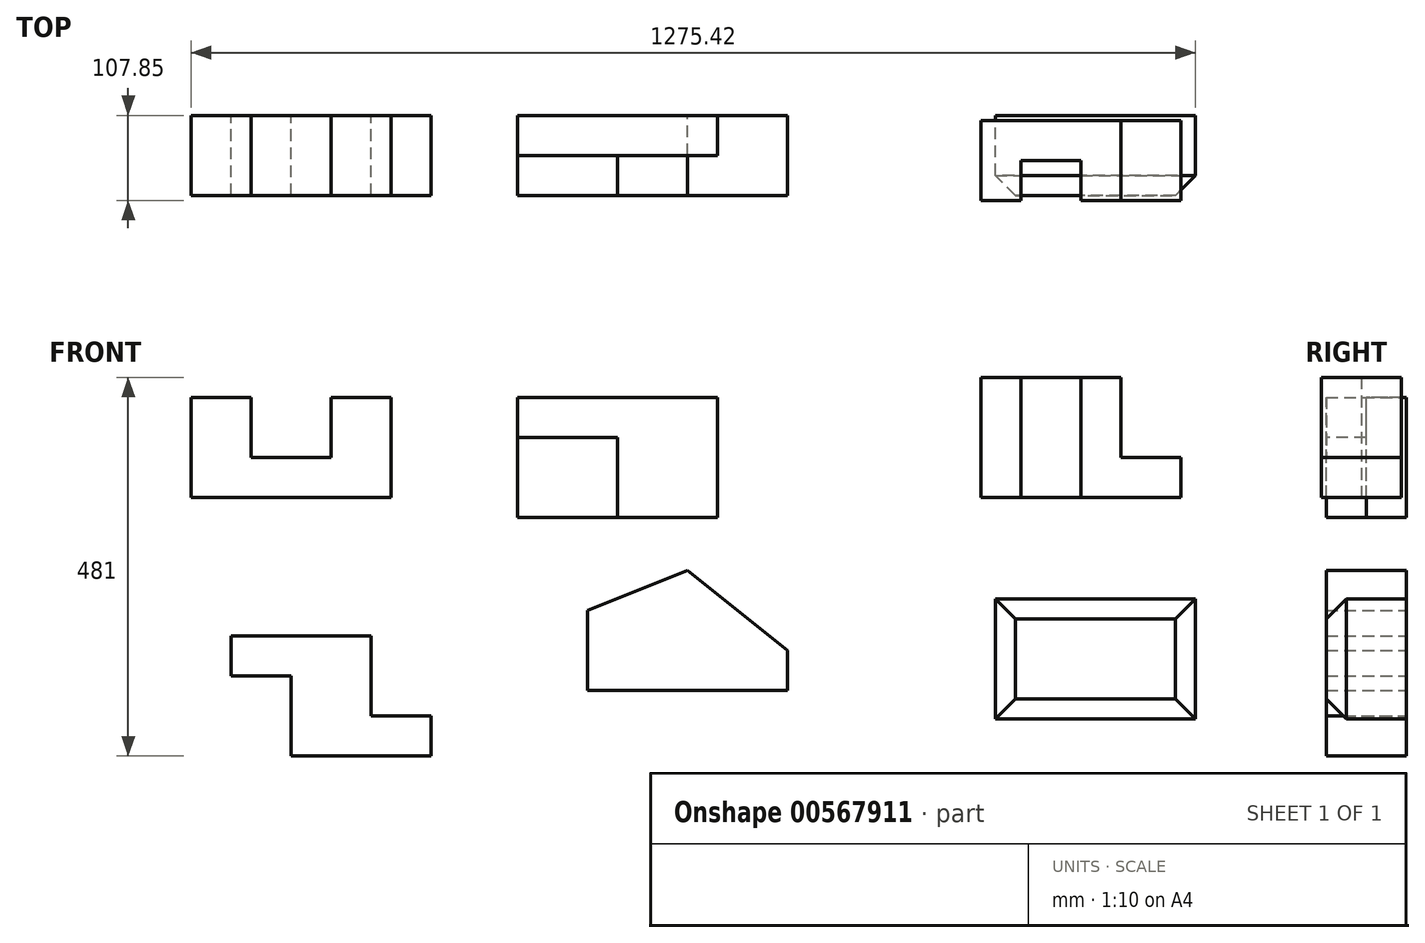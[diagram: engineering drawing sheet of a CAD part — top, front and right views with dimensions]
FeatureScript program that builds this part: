
annotation { "Feature Type Name" : "Feature", "Feature Type Description" : "" }
export const myFeature = defineFeature(function(context is Context, id is Id, definition is map)
    precondition{}
    {
        {
            var Q0;
            Q0=qCreatedBy(makeId("Front.planeOp"),FACE);
            var sketch = newSketch(context, id + "F0", { "sketchPlane" : qUnion([Q0])});
            skLineSegment(sketch, "E0", {"start": v(0, 0) * mm, "end": v(127, 0) * mm});
            skLineSegment(sketch, "E1", {"start": v(0, 0) * mm, "end": v(-127, 0) * mm});
            skLineSegment(sketch, "E2", {"start": v(-127, 0) * mm, "end": v(-127, 127) * mm});
            skLineSegment(sketch, "E3", {"start": v(127, 0) * mm, "end": v(127, 127) * mm});
            skLineSegment(sketch, "E4", {"start": v(-127, 127) * mm, "end": v(-50.8, 127) * mm});
            skLineSegment(sketch, "E5", {"start": v(-50.8, 127) * mm, "end": v(-50.8, 50.8) * mm});
            skLineSegment(sketch, "E6", {"start": v(127, 127) * mm, "end": v(50.8, 127) * mm});
            skLineSegment(sketch, "E7", {"start": v(50.8, 127) * mm, "end": v(50.8, 50.8) * mm});
            skLineSegment(sketch, "E8", {"start": v(-50.8, 50.8) * mm, "end": v(50.8, 50.8) * mm});
            skSolve(sketch);
        }
        {
            var Q0;
            Q0 = qSketchRegion(id + "F0", true);
            extrude(context, id + "F1", {"entities" : qUnion([Q0]), "depth" : 101.6 * mm, "offsetDistance" : 25.4 * mm});
        }
        {
            var Q0;
            Q0=makeQuery(id+"F1.opExtrude","SWEPT_FACE",FACE,{"disambiguationData":[OSD([sQuery(id+"F0.wireOp",EDGE,"E4")])]});
            var sketch = newSketch(context, id + "F2", { "sketchPlane" : qUnion([Q0])});
            skLineSegment(sketch, "E9", {"start": v(287.62, 0) * mm, "end": v(287.62, -101.6) * mm});
            skLineSegment(sketch, "E10", {"start": v(287.62, 0) * mm, "end": v(541.62, 0) * mm});
            skLineSegment(sketch, "E11", {"start": v(541.62, 0) * mm, "end": v(541.62, -50.8) * mm});
            skLineSegment(sketch, "E12", {"start": v(541.62, -50.8) * mm, "end": v(414.62, -50.8) * mm});
            skLineSegment(sketch, "E13", {"start": v(414.62, -50.8) * mm, "end": v(414.62, -101.6) * mm});
            skLineSegment(sketch, "E14", {"start": v(414.62, -101.6) * mm, "end": v(287.62, -101.6) * mm});
            skSolve(sketch);
        }
        {
            var Q0;
            Q0=makeQuery(id+"F2.imprint","IMPRINT",FACE,{"disambiguationData":[TD([[makeQuery(id+"F2.imprint","IMPRINT",EDGE,{"derivedFrom":sQuery(id+"F2.wireOp",EDGE,"E9")}),1.0]])]});
            extrude(context, id + "F3", {"entities" : qUnion([Q0]), "oppositeDirection" : true, "depth" : 152.4 * mm, "offsetDistance" : 25.4 * mm});
        }
        {
            var Q0;
            Q0=makeQuery(id+"F3.opExtrude","SWEPT_FACE",FACE,{"disambiguationData":[OSD([sQuery(id+"F2.wireOp",EDGE,"E14")])]});
            var sketch = newSketch(context, id + "F4", { "sketchPlane" : qUnion([Q0])});
            skLineSegment(sketch, "E15.bottom", {"start": v(287.62, 127) * mm, "end": v(414.62, 127) * mm});
            skLineSegment(sketch, "E15.top", {"start": v(287.62, 76.2) * mm, "end": v(414.62, 76.2) * mm});
            skLineSegment(sketch, "E15.left", {"start": v(287.62, 127) * mm, "end": v(287.62, 76.2) * mm});
            skLineSegment(sketch, "E15.right", {"start": v(414.62, 127) * mm, "end": v(414.62, 76.2) * mm});
            skSolve(sketch);
        }
        {
            var Q0;
            Q0=makeQuery(id+"F4.imprint","IMPRINT",FACE,{"disambiguationData":[TD([[makeQuery(id+"F4.imprint","IMPRINT",EDGE,{"derivedFrom":sQuery(id+"F4.wireOp",EDGE,"E15.bottom")}),1.0]])]});
            extrude(context, id + "F5", {"entities" : qUnion([Q0]), "operationType" : NewBodyOperationType.REMOVE, "oppositeDirection" : true, "depth" : 50.8 * mm, "offsetDistance" : 25.4 * mm});
        }
        {
            var Q0;
            Q0=qCreatedBy(makeId("Top.planeOp"),FACE);
            var sketch = newSketch(context, id + "F6", { "sketchPlane" : qUnion([Q0])});
            skLineSegment(sketch, "E16", {"start": v(875.87, -6.25) * mm, "end": v(875.87, -107.85) * mm});
            skLineSegment(sketch, "E17", {"start": v(875.87, -6.25) * mm, "end": v(1129.87, -6.25) * mm});
            skLineSegment(sketch, "E18", {"start": v(1129.87, -6.25) * mm, "end": v(1129.87, -107.85) * mm});
            skLineSegment(sketch, "E19", {"start": v(1129.87, -107.85) * mm, "end": v(1002.87, -107.85) * mm});
            skLineSegment(sketch, "E20", {"start": v(1002.87, -107.85) * mm, "end": v(1002.87, -57.05) * mm});
            skLineSegment(sketch, "E21", {"start": v(1002.87, -57.05) * mm, "end": v(926.67, -57.05) * mm});
            skLineSegment(sketch, "E22", {"start": v(926.67, -57.05) * mm, "end": v(926.67, -107.85) * mm});
            skLineSegment(sketch, "E23", {"start": v(926.67, -107.85) * mm, "end": v(875.87, -107.85) * mm});
            skSolve(sketch);
        }
        {
            var Q0;
            Q0 = qSketchRegion(id + "F6", true);
            extrude(context, id + "F7", {"entities" : qUnion([Q0]), "depth" : 152.4 * mm, "offsetDistance" : 25.4 * mm});
        }
        {
            var Q0;
            Q0=makeQuery(id+"F7.opExtrude","CAP_FACE",FACE,{"disambiguationData":[OSD([sQuery(id+"F6.wireOp",EDGE,"E16"),sQuery(id+"F6.wireOp",EDGE,"E17"),sQuery(id+"F6.wireOp",EDGE,"E18"),sQuery(id+"F6.wireOp",EDGE,"E19"),sQuery(id+"F6.wireOp",EDGE,"E20"),sQuery(id+"F6.wireOp",EDGE,"E21"),sQuery(id+"F6.wireOp",EDGE,"E22"),sQuery(id+"F6.wireOp",EDGE,"E23")])],"isStart":false});
            var sketch = newSketch(context, id + "F8", { "sketchPlane" : qUnion([Q0])});
            skLineSegment(sketch, "E24.bottom", {"start": v(1129.87, -107.85) * mm, "end": v(1053.67, -107.85) * mm});
            skLineSegment(sketch, "E24.top", {"start": v(1129.87, -6.25) * mm, "end": v(1053.67, -6.25) * mm});
            skLineSegment(sketch, "E24.left", {"start": v(1129.87, -107.85) * mm, "end": v(1129.87, -6.25) * mm});
            skLineSegment(sketch, "E24.right", {"start": v(1053.67, -107.85) * mm, "end": v(1053.67, -6.25) * mm});
            skSolve(sketch);
        }
        {
            var Q0;
            Q0=makeQuery(id+"F8.imprint","IMPRINT",FACE,{"disambiguationData":[TD([[makeQuery(id+"F8.imprint","IMPRINT",EDGE,{"derivedFrom":sQuery(id+"F8.wireOp",EDGE,"E24.bottom")}),-1.0]])]});
            extrude(context, id + "F9", {"entities" : qUnion([Q0]), "operationType" : NewBodyOperationType.REMOVE, "oppositeDirection" : true, "depth" : 101.6 * mm, "offsetDistance" : 25.4 * mm});
        }
        {
            var Q0;
            Q0=qCreatedBy(makeId("Front.planeOp"),FACE);
            var sketch = newSketch(context, id + "F10", { "sketchPlane" : qUnion([Q0])});
            skLineSegment(sketch, "E25", {"start": v(-76.2, -176.2) * mm, "end": v(101.6, -176.2) * mm});
            skLineSegment(sketch, "E26", {"start": v(-76.2, -176.2) * mm, "end": v(-76.2, -227) * mm});
            skLineSegment(sketch, "E27", {"start": v(101.6, -176.2) * mm, "end": v(101.6, -277.8) * mm});
            skLineSegment(sketch, "E28", {"start": v(101.6, -277.8) * mm, "end": v(177.8, -277.8) * mm});
            skLineSegment(sketch, "E29", {"start": v(177.8, -277.8) * mm, "end": v(177.8, -328.6) * mm});
            skLineSegment(sketch, "E30", {"start": v(177.8, -328.6) * mm, "end": v(0, -328.6) * mm});
            skLineSegment(sketch, "E31", {"start": v(0, -328.6) * mm, "end": v(0, -227) * mm});
            skLineSegment(sketch, "E32", {"start": v(0, -227) * mm, "end": v(-76.2, -227) * mm});
            skSolve(sketch);
        }
        {
            var Q0;
            Q0 = qSketchRegion(id + "F10", true);
            extrude(context, id + "F11", {"entities" : qUnion([Q0]), "depth" : 101.6 * mm, "offsetDistance" : 25.4 * mm});
        }
        {
            var Q0;
            Q0=qCreatedBy(makeId("Front.planeOp"),FACE);
            var sketch = newSketch(context, id + "F12", { "sketchPlane" : qUnion([Q0])});
            skLineSegment(sketch, "E33", {"start": v(376.35, -143.63) * mm, "end": v(376.35, -245.23) * mm});
            skLineSegment(sketch, "E34", {"start": v(376.35, -245.23) * mm, "end": v(630.35, -245.23) * mm});
            skLineSegment(sketch, "E35", {"start": v(630.35, -245.23) * mm, "end": v(630.35, -194.43) * mm});
            skLineSegment(sketch, "E36", {"start": v(376.35, -143.63) * mm, "end": v(503.35, -92.83) * mm});
            skLineSegment(sketch, "E37", {"start": v(503.35, -92.83) * mm, "end": v(630.35, -194.43) * mm});
            skSolve(sketch);
        }
        {
            var Q0;
            Q0=makeQuery(id+"F12.imprint","IMPRINT",FACE,{"disambiguationData":[TD([[makeQuery(id+"F12.imprint","IMPRINT",EDGE,{"derivedFrom":sQuery(id+"F12.wireOp",EDGE,"E33")}),1.0]])]});
            extrude(context, id + "F13", {"entities" : qUnion([Q0]), "depth" : 101.6 * mm, "offsetDistance" : 25.4 * mm});
        }
        {
            var Q0;
            Q0=qCreatedBy(makeId("Front.planeOp"),FACE);
            var sketch = newSketch(context, id + "F14", { "sketchPlane" : qUnion([Q0])});
            skLineSegment(sketch, "E38.bottom", {"start": v(894.42, -128.97) * mm, "end": v(1148.42, -128.97) * mm});
            skLineSegment(sketch, "E38.top", {"start": v(894.42, -281.37) * mm, "end": v(1148.42, -281.37) * mm});
            skLineSegment(sketch, "E38.left", {"start": v(894.42, -128.97) * mm, "end": v(894.42, -281.37) * mm});
            skLineSegment(sketch, "E38.right", {"start": v(1148.42, -128.97) * mm, "end": v(1148.42, -281.37) * mm});
            skSolve(sketch);
        }
        {
            var Q0;
            Q0 = qSketchRegion(id + "F14", true);
            extrude(context, id + "F15", {"entities" : qUnion([Q0]), "depth" : 101.6 * mm, "offsetDistance" : 25.4 * mm});
        }
        {
            var Q0;
            Q0=makeQuery(id+"F15.opExtrude","CAP_EDGE",EDGE,{"disambiguationData":[OSD([sQuery(id+"F14.wireOp",EDGE,"E38.bottom")])],"isStart":false});
            var Q1;
            Q1=makeQuery(id+"F15.opExtrude","CAP_EDGE",EDGE,{"disambiguationData":[OSD([sQuery(id+"F14.wireOp",EDGE,"E38.right")])],"isStart":false});
            var Q2;
            Q2=makeQuery(id+"F15.opExtrude","CAP_EDGE",EDGE,{"disambiguationData":[OSD([sQuery(id+"F14.wireOp",EDGE,"E38.left")])],"isStart":false});
            var Q3;
            Q3=makeQuery(id+"F15.opExtrude","CAP_EDGE",EDGE,{"disambiguationData":[OSD([sQuery(id+"F14.wireOp",EDGE,"E38.top")])],"isStart":false});
            chamfer(context, id + "F16", {"entities" : qUnion([Q0, Q1, Q2, Q3]), "width" : 25.4 * mm, "tangentPropagation" : true});
        }
    });
